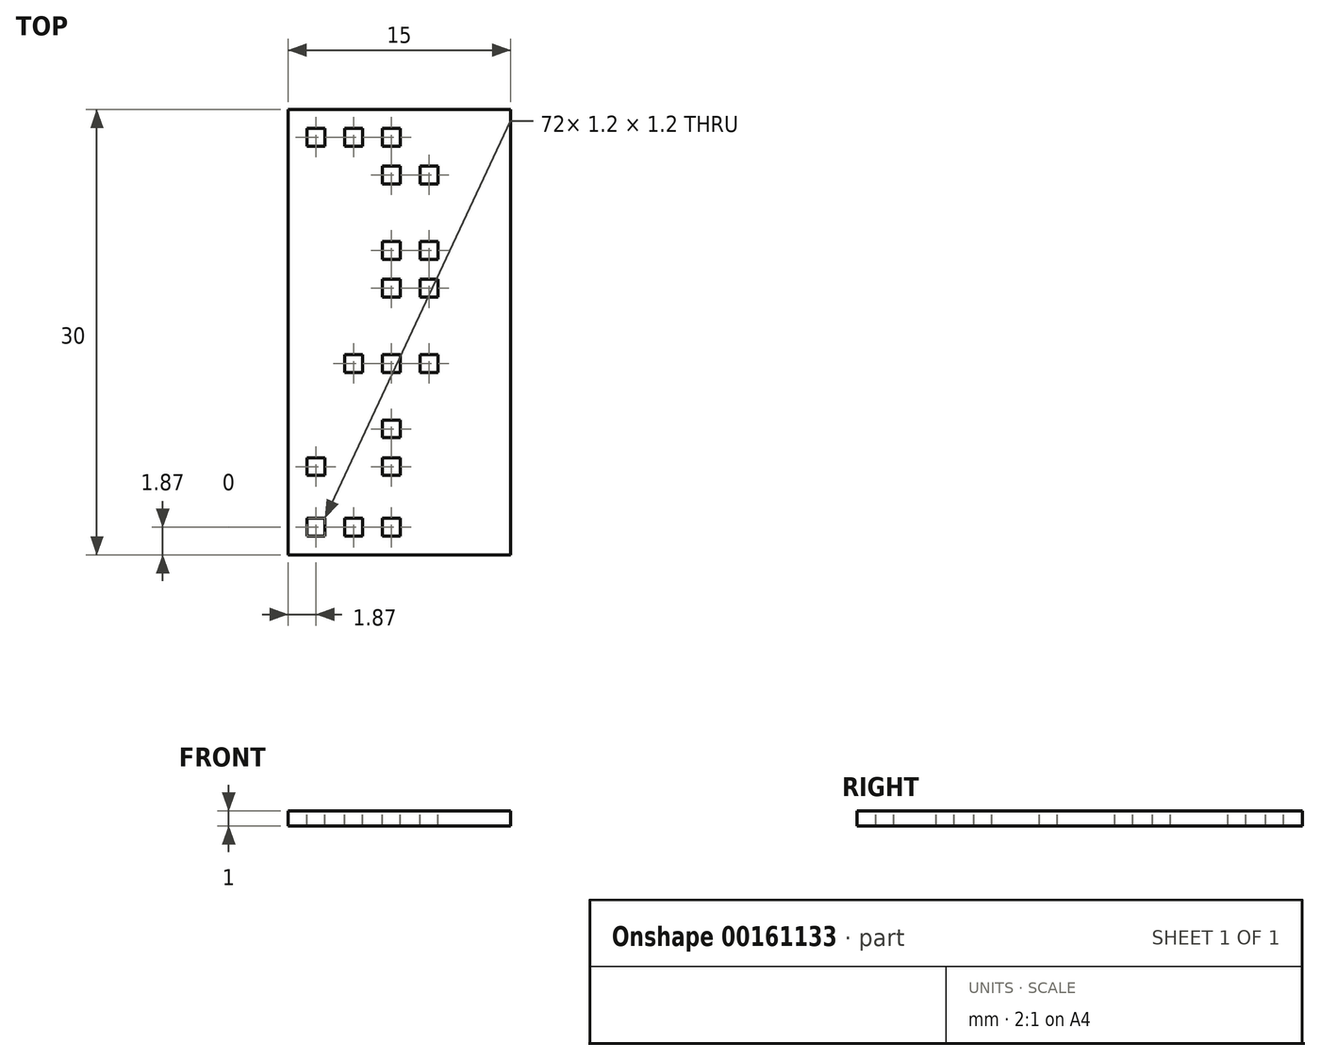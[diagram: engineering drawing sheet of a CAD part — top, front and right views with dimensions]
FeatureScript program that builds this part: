
annotation { "Feature Type Name" : "Feature", "Feature Type Description" : "" }
export const myFeature = defineFeature(function(context is Context, id is Id, definition is map)
    precondition{}
    {
        {
            var Q0;
            Q0=qCreatedBy(makeId("Top.planeOp"),FACE);
            var sketch = newSketch(context, id + "F0", { "sketchPlane" : qUnion([Q0])});
            skLineSegment(sketch, "E0.bottom", {"start": v(-15, 30) * mm, "end": v(0, 30) * mm});
            skLineSegment(sketch, "E0.top", {"start": v(-15, 0) * mm, "end": v(0, 0) * mm});
            skLineSegment(sketch, "E0.left", {"start": v(-15, 30) * mm, "end": v(-15, 0) * mm});
            skLineSegment(sketch, "E0.right", {"start": v(0, 30) * mm, "end": v(0, 0) * mm});
            skSolve(sketch);
        }
        {
            var Q0;
            Q0 = qSketchRegion(id + "F0", true);
            extrude(context, id + "F1", {"entities" : qUnion([Q0]), "depth" : 1 * mm});
        }
        {
            var Q0;
            Q0=makeQuery(id+"F1.opExtrude","CAP_FACE",FACE,{"disambiguationData":[OSD([sQuery(id+"F0.wireOp",EDGE,"E0.bottom"),sQuery(id+"F0.wireOp",EDGE,"E0.top"),sQuery(id+"F0.wireOp",EDGE,"E0.left"),sQuery(id+"F0.wireOp",EDGE,"E0.right")])],"isStart":false});
            var sketch = newSketch(context, id + "F2", { "sketchPlane" : qUnion([Q0])});
            skLineSegment(sketch, "E1.bottom", {"start": v(-13.73, 28.73) * mm, "end": v(-12.53, 28.73) * mm});
            skLineSegment(sketch, "E1.top", {"start": v(-13.73, 27.53) * mm, "end": v(-12.53, 27.53) * mm});
            skLineSegment(sketch, "E1.left", {"start": v(-13.73, 28.73) * mm, "end": v(-13.73, 27.53) * mm});
            skLineSegment(sketch, "E1.right", {"start": v(-12.53, 28.73) * mm, "end": v(-12.53, 27.53) * mm});
            skLineSegment(sketch, "E2.bottom", {"start": v(-11.19, 28.73) * mm, "end": v(-9.99, 28.73) * mm});
            skLineSegment(sketch, "E2.top", {"start": v(-11.19, 27.53) * mm, "end": v(-9.99, 27.53) * mm});
            skLineSegment(sketch, "E2.left", {"start": v(-11.19, 28.73) * mm, "end": v(-11.19, 27.53) * mm});
            skLineSegment(sketch, "E2.right", {"start": v(-9.99, 28.73) * mm, "end": v(-9.99, 27.53) * mm});
            skLineSegment(sketch, "E3.bottom", {"start": v(-8.65, 28.73) * mm, "end": v(-7.45, 28.73) * mm});
            skLineSegment(sketch, "E3.top", {"start": v(-8.65, 27.53) * mm, "end": v(-7.45, 27.53) * mm});
            skLineSegment(sketch, "E3.left", {"start": v(-8.65, 28.73) * mm, "end": v(-8.65, 27.53) * mm});
            skLineSegment(sketch, "E3.right", {"start": v(-7.45, 28.73) * mm, "end": v(-7.45, 27.53) * mm});
            skLineSegment(sketch, "E4.bottom", {"start": v(-8.65, 2.47) * mm, "end": v(-7.45, 2.47) * mm});
            skLineSegment(sketch, "E4.top", {"start": v(-8.65, 1.27) * mm, "end": v(-7.45, 1.27) * mm});
            skLineSegment(sketch, "E4.left", {"start": v(-8.65, 2.47) * mm, "end": v(-8.65, 1.27) * mm});
            skLineSegment(sketch, "E4.right", {"start": v(-7.45, 2.47) * mm, "end": v(-7.45, 1.27) * mm});
            skLineSegment(sketch, "E5.bottom", {"start": v(-11.19, 2.47) * mm, "end": v(-9.99, 2.47) * mm});
            skLineSegment(sketch, "E5.top", {"start": v(-11.19, 1.27) * mm, "end": v(-9.99, 1.27) * mm});
            skLineSegment(sketch, "E5.left", {"start": v(-11.19, 2.47) * mm, "end": v(-11.19, 1.27) * mm});
            skLineSegment(sketch, "E5.right", {"start": v(-9.99, 2.47) * mm, "end": v(-9.99, 1.27) * mm});
            skLineSegment(sketch, "E6.bottom", {"start": v(-13.73, 2.47) * mm, "end": v(-12.53, 2.47) * mm});
            skLineSegment(sketch, "E6.top", {"start": v(-13.73, 1.27) * mm, "end": v(-12.53, 1.27) * mm});
            skLineSegment(sketch, "E6.left", {"start": v(-13.73, 2.47) * mm, "end": v(-13.73, 1.27) * mm});
            skLineSegment(sketch, "E6.right", {"start": v(-12.53, 2.47) * mm, "end": v(-12.53, 1.27) * mm});
            skLineSegment(sketch, "E7.bottom", {"start": v(-8.65, 26.2) * mm, "end": v(-7.45, 26.2) * mm});
            skLineSegment(sketch, "E7.top", {"start": v(-8.65, 25) * mm, "end": v(-7.45, 25) * mm});
            skLineSegment(sketch, "E7.left", {"start": v(-8.65, 26.2) * mm, "end": v(-8.65, 25) * mm});
            skLineSegment(sketch, "E7.right", {"start": v(-7.45, 26.2) * mm, "end": v(-7.45, 25) * mm});
            skLineSegment(sketch, "E8.bottom", {"start": v(-8.65, 21.11) * mm, "end": v(-7.45, 21.11) * mm});
            skLineSegment(sketch, "E8.top", {"start": v(-8.65, 19.91) * mm, "end": v(-7.45, 19.91) * mm});
            skLineSegment(sketch, "E8.left", {"start": v(-8.65, 21.11) * mm, "end": v(-8.65, 19.91) * mm});
            skLineSegment(sketch, "E8.right", {"start": v(-7.45, 21.11) * mm, "end": v(-7.45, 19.91) * mm});
            skLineSegment(sketch, "E9.bottom", {"start": v(-8.65, 18.57) * mm, "end": v(-7.45, 18.57) * mm});
            skLineSegment(sketch, "E9.top", {"start": v(-8.65, 17.37) * mm, "end": v(-7.45, 17.37) * mm});
            skLineSegment(sketch, "E9.left", {"start": v(-8.65, 18.57) * mm, "end": v(-8.65, 17.37) * mm});
            skLineSegment(sketch, "E9.right", {"start": v(-7.45, 18.57) * mm, "end": v(-7.45, 17.37) * mm});
            skLineSegment(sketch, "E10.bottom", {"start": v(-8.65, 13.5) * mm, "end": v(-7.45, 13.5) * mm});
            skLineSegment(sketch, "E10.top", {"start": v(-8.65, 12.3) * mm, "end": v(-7.45, 12.3) * mm});
            skLineSegment(sketch, "E10.left", {"start": v(-8.65, 13.5) * mm, "end": v(-8.65, 12.3) * mm});
            skLineSegment(sketch, "E10.right", {"start": v(-7.45, 13.5) * mm, "end": v(-7.45, 12.3) * mm});
            skLineSegment(sketch, "E11.bottom", {"start": v(-6.1, 26.2) * mm, "end": v(-4.9, 26.2) * mm});
            skLineSegment(sketch, "E11.top", {"start": v(-6.1, 25) * mm, "end": v(-4.9, 25) * mm});
            skLineSegment(sketch, "E11.left", {"start": v(-6.1, 26.2) * mm, "end": v(-6.1, 25) * mm});
            skLineSegment(sketch, "E11.right", {"start": v(-4.9, 26.2) * mm, "end": v(-4.9, 25) * mm});
            skLineSegment(sketch, "E12.bottom", {"start": v(-6.1, 21.11) * mm, "end": v(-4.9, 21.11) * mm});
            skLineSegment(sketch, "E12.top", {"start": v(-6.1, 19.91) * mm, "end": v(-4.9, 19.91) * mm});
            skLineSegment(sketch, "E12.left", {"start": v(-6.1, 21.11) * mm, "end": v(-6.1, 19.91) * mm});
            skLineSegment(sketch, "E12.right", {"start": v(-4.9, 21.11) * mm, "end": v(-4.9, 19.91) * mm});
            skLineSegment(sketch, "E13", {"start": v(-8.05, 27.53) * mm, "end": v(-8.05, 26.2) * mm, "construction": true});
            skLineSegment(sketch, "E14", {"start": v(-8.05, 27.53) * mm, "end": v(-5.51, 26.2) * mm, "construction": true});
            skLineSegment(sketch, "E15", {"start": v(-5.5, 19.91) * mm, "end": v(-8.05, 18.57) * mm, "construction": true});
            skLineSegment(sketch, "E16", {"start": v(-8.05, 19.91) * mm, "end": v(-6.78, 19.24) * mm, "construction": true});
            skLineSegment(sketch, "E17", {"start": v(-10.59, 27.53) * mm, "end": v(-10.59, 19.24) * mm, "construction": true});
            skLineSegment(sketch, "E18", {"start": v(-10.59, 19.24) * mm, "end": v(-6.78, 19.24) * mm, "construction": true});
            skLineSegment(sketch, "E19.bottom", {"start": v(-6.1, 18.57) * mm, "end": v(-4.9, 18.57) * mm});
            skLineSegment(sketch, "E19.top", {"start": v(-6.1, 17.37) * mm, "end": v(-4.9, 17.37) * mm});
            skLineSegment(sketch, "E19.left", {"start": v(-6.1, 18.57) * mm, "end": v(-6.1, 17.37) * mm});
            skLineSegment(sketch, "E19.right", {"start": v(-4.9, 18.57) * mm, "end": v(-4.9, 17.37) * mm});
            skLineSegment(sketch, "E20.bottom", {"start": v(-6.1, 13.5) * mm, "end": v(-4.9, 13.5) * mm});
            skLineSegment(sketch, "E20.top", {"start": v(-6.1, 12.3) * mm, "end": v(-4.9, 12.3) * mm});
            skLineSegment(sketch, "E20.left", {"start": v(-6.1, 13.5) * mm, "end": v(-6.1, 12.3) * mm});
            skLineSegment(sketch, "E20.right", {"start": v(-4.9, 13.5) * mm, "end": v(-4.9, 12.3) * mm});
            skLineSegment(sketch, "E21", {"start": v(-6.78, 19.24) * mm, "end": v(-5.5, 18.57) * mm, "construction": true});
            skLineSegment(sketch, "E22.bottom", {"start": v(-11.19, 13.5) * mm, "end": v(-9.99, 13.5) * mm});
            skLineSegment(sketch, "E22.top", {"start": v(-11.19, 12.3) * mm, "end": v(-9.99, 12.3) * mm});
            skLineSegment(sketch, "E22.left", {"start": v(-11.19, 13.5) * mm, "end": v(-11.19, 12.3) * mm});
            skLineSegment(sketch, "E22.right", {"start": v(-9.99, 13.5) * mm, "end": v(-9.99, 12.3) * mm});
            skLineSegment(sketch, "E23.bottom", {"start": v(-8.65, 9.1) * mm, "end": v(-7.45, 9.1) * mm});
            skLineSegment(sketch, "E23.top", {"start": v(-8.65, 7.9) * mm, "end": v(-7.45, 7.9) * mm});
            skLineSegment(sketch, "E23.left", {"start": v(-8.65, 9.1) * mm, "end": v(-8.65, 7.9) * mm});
            skLineSegment(sketch, "E23.right", {"start": v(-7.45, 9.1) * mm, "end": v(-7.45, 7.9) * mm});
            skLineSegment(sketch, "E24.bottom", {"start": v(-13.73, 6.55) * mm, "end": v(-12.53, 6.55) * mm});
            skLineSegment(sketch, "E24.top", {"start": v(-13.73, 5.35) * mm, "end": v(-12.53, 5.35) * mm});
            skLineSegment(sketch, "E24.left", {"start": v(-13.73, 6.55) * mm, "end": v(-13.73, 5.35) * mm});
            skLineSegment(sketch, "E24.right", {"start": v(-12.53, 6.55) * mm, "end": v(-12.53, 5.35) * mm});
            skLineSegment(sketch, "E25.bottom", {"start": v(-8.65, 6.55) * mm, "end": v(-7.45, 6.55) * mm});
            skLineSegment(sketch, "E25.top", {"start": v(-8.65, 5.35) * mm, "end": v(-7.45, 5.35) * mm});
            skLineSegment(sketch, "E25.left", {"start": v(-8.65, 6.55) * mm, "end": v(-8.65, 5.35) * mm});
            skLineSegment(sketch, "E25.right", {"start": v(-7.45, 6.55) * mm, "end": v(-7.45, 5.35) * mm});
            skLineSegment(sketch, "E26", {"start": v(-8.05, 12.3) * mm, "end": v(-8.05, 9.1) * mm, "construction": true});
            skLineSegment(sketch, "E27", {"start": v(-5.5, 12.3) * mm, "end": v(-8.05, 9.1) * mm, "construction": true});
            skLineSegment(sketch, "E28", {"start": v(-8.05, 7.9) * mm, "end": v(-8.05, 6.55) * mm, "construction": true});
            skLineSegment(sketch, "E29", {"start": v(-8.05, 5.35) * mm, "end": v(-8.05, 2.47) * mm, "construction": true});
            skLineSegment(sketch, "E30", {"start": v(-13.13, 27.53) * mm, "end": v(-13.13, 6.55) * mm, "construction": true});
            skLineSegment(sketch, "E31", {"start": v(-13.13, 5.35) * mm, "end": v(-13.13, 2.47) * mm, "construction": true});
            skLineSegment(sketch, "E32", {"start": v(-10.59, 19.24) * mm, "end": v(-10.59, 13.5) * mm, "construction": true});
            skLineSegment(sketch, "E33", {"start": v(-10.59, 12.3) * mm, "end": v(-10.59, 2.47) * mm, "construction": true});
            skSolve(sketch);
        }
        {
            var Q0;
            Q0 = qSketchRegion(id + "F2", true);
            extrude(context, id + "F3", {"entities" : qUnion([Q0]), "operationType" : NewBodyOperationType.REMOVE, "oppositeDirection" : true, "depth" : 25 * mm});
        }
    });
